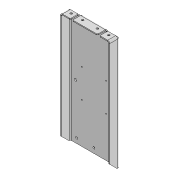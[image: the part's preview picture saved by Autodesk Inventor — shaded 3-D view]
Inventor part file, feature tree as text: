
AUTODESK INVENTOR PART (.ipt)
format: ipt  version: 2020 (Build 240168000, 168)  size: 233,472 bytes
history: native  units: mm
features: other x14, sketch x9, hole x4, projected_geometry x2, extrude x1, chamfer x1, fillet x1
ambient origin geometry x8: Origin, YZ Plane, XZ Plane, XY Plane, X Axis, Y Axis, Z Axis, Center Point
bodies: Body1 (feature_tree)
feature tree (32):
  other  "ソリッド1"
  other  "フランジ1"
  other  "フランジ5"
  extrude  "押し出し1"  Depth=100.0mm
  other  "フランジ6"
  hole  "穴1"  [1 undecoded]
  chamfer  "面取り1"  Distance=227.0mm
  hole  "穴2"  [1 undecoded]
  fillet  "フィレット1"  Radius=2.0mm
  hole  "穴3"  [1 undecoded]
  hole  "穴4"  [1 undecoded]
  sketch  "スケッチ1"
  other  "プレート1"
  sketch  "スケッチ2"
  other  "プレート2"
  other  "曲げ1"
  other  "コーナー1"
  sketch  "スケッチ6"
  other  "プレート6"
  other  "曲げ5"
  other  "コーナー5"
  sketch  "スケッチ7"
  sketch  "スケッチ8"
  other  "プレート7"
  other  "曲げ6"
  other  "コーナー6"
  sketch  "スケッチ9"
  sketch  "スケッチ10"
  sketch  "スケッチ12"
  projected_geometry  "投影ループ1"
  sketch  "スケッチ13"
  projected_geometry  "投影ループ2"
note: 4 required parameter values undecoded (feature->parameter linkage not recoverable at this tier; creation-order binding heuristic only, values carry confidence <= 0.55)
